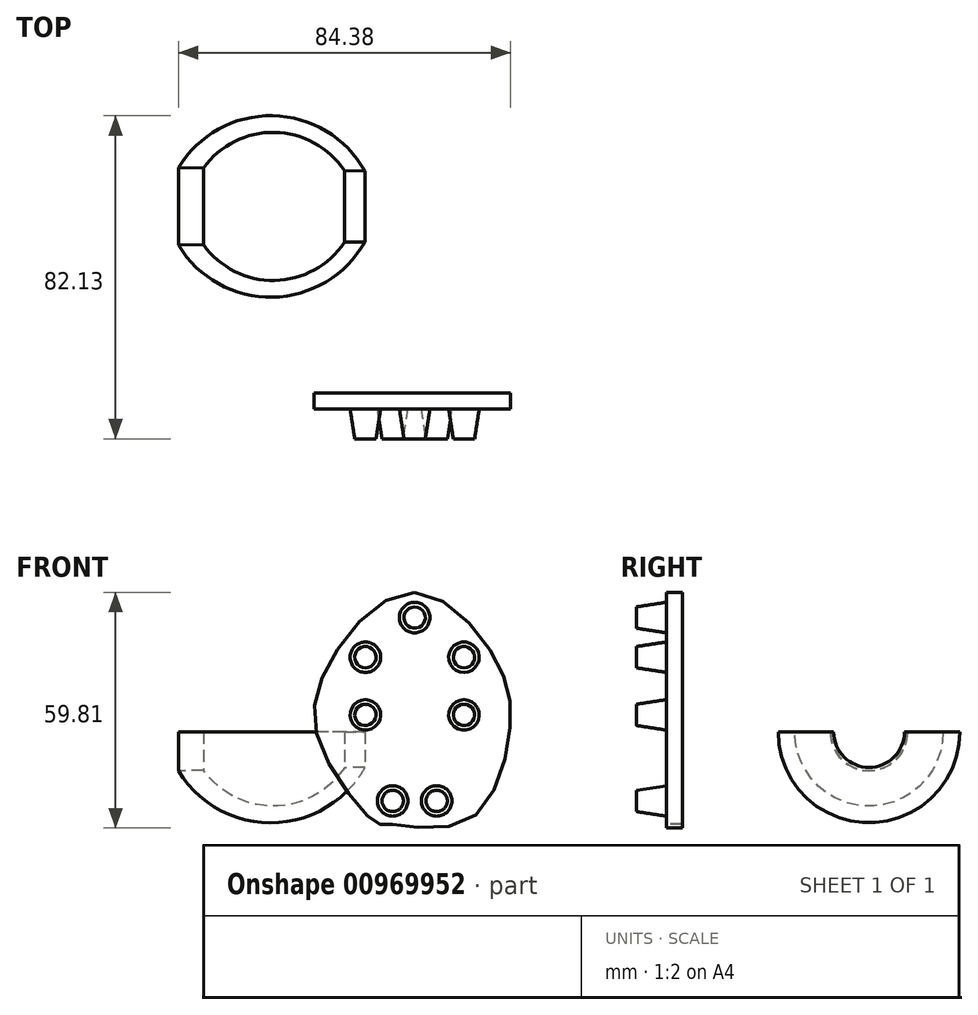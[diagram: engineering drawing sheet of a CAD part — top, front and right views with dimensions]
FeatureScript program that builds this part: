
annotation { "Feature Type Name" : "Feature", "Feature Type Description" : "" }
export const myFeature = defineFeature(function(context is Context, id is Id, definition is map)
    precondition{}
    {
        {
            var Q0;
            Q0=qCreatedBy(makeId("Front.planeOp"),FACE);
            var sketch = newSketch(context, id + "F0", { "sketchPlane" : qUnion([Q0])});
            skCircle(sketch, "E0", {"center": v(0, 29.08) * mm, "radius": 3.88 * mm});
            skSolve(sketch);
        }
        {
            var Q0;
            Q0=qCreatedBy(makeId("Front.planeOp"),FACE);
            cPlane(context, id + "F1", {"entities" : qUnion([Q0]), "cplaneType" : CPlaneType.OFFSET, "offset" : 25.4 * mm, "width" : 152.4 * mm, "height" : 152.4 * mm});
        }
        {
            var Q0;
            Q0=qCreatedBy(id+"F1.planeOp",FACE);
            var sketch = newSketch(context, id + "F2", { "sketchPlane" : qUnion([Q0])});
            skCircle(sketch, "E1", {"center": v(0, 29.1) * mm, "radius": 1.18 * mm});
            skSolve(sketch);
        }
        {
            var Q0;
            Q0=makeQuery(id+"F0.imprint","IMPRINT",FACE,{"disambiguationData":[TD([[makeQuery(id+"F0.imprint","IMPRINT",EDGE,{"derivedFrom":sQuery(id+"F0.wireOp",EDGE,"E0")}),1.0]])]});
            var Q1;
            Q1=sQuery(id+"F2.wireOp",VERTEX,"E1.center");
            loft(context, id + "F3", {"sheetProfilesArray" : [{ "sheetProfileEntities" : qUnion([Q0]) }, { "sheetProfileEntities" : qUnion([Q1]) }]});
        }
        {
            var Q0;
            Q0=qCreatedBy(id+"F1.planeOp",FACE);
            cPlane(context, id + "F4", {"entities" : qUnion([Q0]), "cplaneType" : CPlaneType.OFFSET, "offset" : 17.78 * mm, "oppositeDirection" : true, "width" : 152.4 * mm, "height" : 152.4 * mm});
        }
        {
            var Q0;
            Q0=qCreatedBy(id+"F4.planeOp",FACE);
            var sketch = newSketch(context, id + "F5", { "sketchPlane" : qUnion([Q0])});
            skCircle(sketch, "E2", {"center": v(0, 28.47) * mm, "radius": 5.7 * mm});
            skSolve(sketch);
        }
        {
            var Q0;
            Q0=qCreatedBy(id+"F1.planeOp",FACE);
            var sketch = newSketch(context, id + "F6", { "sketchPlane" : qUnion([Q0])});
            skCircle(sketch, "E3", {"center": v(0, 29.1) * mm, "radius": 3.66 * mm});
            skSolve(sketch);
        }
        {
            var Q1;
            Q1=makeQuery(id+"F5.imprint","IMPRINT",FACE,{"disambiguationData":[TD([[makeQuery(id+"F5.imprint","IMPRINT",EDGE,{"derivedFrom":sQuery(id+"F5.wireOp",EDGE,"E2")}),1.0]])]});
            var Q2;
            Q2=makeQuery(id+"F6.imprint","IMPRINT",FACE,{"disambiguationData":[TD([[makeQuery(id+"F6.imprint","IMPRINT",EDGE,{"derivedFrom":sQuery(id+"F6.wireOp",EDGE,"E3")}),1.0]])]});
            loft(context, id + "F7", {"operationType" : NewBodyOperationType.REMOVE, "sheetProfilesArray" : [{ "sheetProfileEntities" : qUnion([Q1]) }, { "sheetProfileEntities" : qUnion([Q2]) }]});
        }
        {
            var Q0;
            Q0=qCreatedBy(makeId("Front.planeOp"),FACE);
            var sketch = newSketch(context, id + "F8", { "sketchPlane" : qUnion([Q0])});
            skCircle(sketch, "E4", {"center": v(-12.51, 19) * mm, "radius": 3.87 * mm});
            skSolve(sketch);
        }
        {
            var Q0;
            Q0=qCreatedBy(id+"F1.planeOp",FACE);
            var sketch = newSketch(context, id + "F9", { "sketchPlane" : qUnion([Q0])});
            skCircle(sketch, "E5", {"center": v(-12.52, 19.02) * mm, "radius": 3.65 * mm});
            skSolve(sketch);
        }
        {
            var Q0;
            Q0=makeQuery(id+"F8.imprint","IMPRINT",FACE,{"disambiguationData":[TD([[makeQuery(id+"F8.imprint","IMPRINT",EDGE,{"derivedFrom":sQuery(id+"F8.wireOp",EDGE,"E4")}),1.0]])]});
            var Q1;
            Q1=sQuery(id+"F9.wireOp",VERTEX,"E5.center");
            loft(context, id + "F10", {"sheetProfilesArray" : [{ "sheetProfileEntities" : qUnion([Q0]) }, { "sheetProfileEntities" : qUnion([Q1]) }]});
        }
        {
            var Q0;
            Q0=qCreatedBy(id+"F4.planeOp",FACE);
            var sketch = newSketch(context, id + "F11", { "sketchPlane" : qUnion([Q0])});
            skCircle(sketch, "E6", {"center": v(-9.74, 19) * mm, "radius": 7.2 * mm});
            skSolve(sketch);
        }
        {
            var Q0;
            Q0=qCreatedBy(id+"F1.planeOp",FACE);
            var sketch = newSketch(context, id + "F12", { "sketchPlane" : qUnion([Q0])});
            skCircle(sketch, "E7", {"center": v(-23.69, 25.05) * mm, "radius": 56.82 * mm});
            skSolve(sketch);
        }
        {
            var Q1;
            Q1=makeQuery(id+"F11.imprint","IMPRINT",FACE,{"disambiguationData":[TD([[makeQuery(id+"F11.imprint","IMPRINT",EDGE,{"derivedFrom":sQuery(id+"F11.wireOp",EDGE,"E6")}),1.0]])]});
            var Q2;
            Q2=makeQuery(id+"F12.imprint","IMPRINT",FACE,{"disambiguationData":[TD([[makeQuery(id+"F12.imprint","IMPRINT",EDGE,{"derivedFrom":sQuery(id+"F12.wireOp",EDGE,"E7")}),1.0]])]});
            loft(context, id + "F13", {"operationType" : NewBodyOperationType.REMOVE, "sheetProfilesArray" : [{ "sheetProfileEntities" : qUnion([Q1]) }, { "sheetProfileEntities" : qUnion([Q2]) }]});
        }
        {
            var Q0;
            Q0=makeQuery(id+"F10.opLoft","SWEPT_BODY",BODY,{"disambiguationData":[OSD([makeQuery(id+"F8.imprint","IMPRINT",FACE,{"disambiguationData":[TD([[makeQuery(id+"F8.imprint","IMPRINT",EDGE,{"derivedFrom":sQuery(id+"F8.wireOp",EDGE,"E4")}),1.0]])]}),sQuery(id+"F9.wireOp",VERTEX,"E5.center")])]});
            var Q1;
            Q1=qCreatedBy(makeId("Right.planeOp"),FACE);
            mirror(context, id + "F14", {"entities" : qUnion([Q0]), "mirrorPlane" : qUnion([Q1])});
        }
        {
            var Q0;
            Q0=qCreatedBy(makeId("Top.planeOp"),FACE);
            cPlane(context, id + "F15", {"entities" : qUnion([Q0]), "cplaneType" : CPlaneType.OFFSET, "offset" : 11.68 * mm, "width" : 152.4 * mm, "height" : 152.4 * mm});
        }
        {
            var Q0;
            Q0=makeQuery(id+"F10.opLoft","SWEPT_BODY",BODY,{"disambiguationData":[OSD([makeQuery(id+"F8.imprint","IMPRINT",FACE,{"disambiguationData":[TD([[makeQuery(id+"F8.imprint","IMPRINT",EDGE,{"derivedFrom":sQuery(id+"F8.wireOp",EDGE,"E4")}),1.0]])]}),sQuery(id+"F9.wireOp",VERTEX,"E5.center")])]});
            var Q1;
            Q1=makeQuery(id+"F14.opPattern","COPY",BODY,{"derivedFrom":makeQuery(id+"F10.opLoft","SWEPT_BODY",BODY,{"disambiguationData":[OSD([makeQuery(id+"F8.imprint","IMPRINT",FACE,{"disambiguationData":[TD([[makeQuery(id+"F8.imprint","IMPRINT",EDGE,{"derivedFrom":sQuery(id+"F8.wireOp",EDGE,"E4")}),1.0]])]}),sQuery(id+"F9.wireOp",VERTEX,"E5.center")])]}),"instanceName":"1"});
            var Q2;
            Q2=qCreatedBy(id+"F15.planeOp",FACE);
            mirror(context, id + "F16", {"entities" : qUnion([Q0, Q1]), "mirrorPlane" : qUnion([Q2])});
        }
        {
            var Q0;
            Q0=qCreatedBy(makeId("Front.planeOp"),FACE);
            var sketch = newSketch(context, id + "F17", { "sketchPlane" : qUnion([Q0])});
            skCircle(sketch, "E8", {"center": v(-5.59, -17.5) * mm, "radius": 3.88 * mm});
            skSolve(sketch);
        }
        {
            var Q0;
            Q0=qCreatedBy(id+"F1.planeOp",FACE);
            var sketch = newSketch(context, id + "F18", { "sketchPlane" : qUnion([Q0])});
            skCircle(sketch, "E9", {"center": v(-5.59, -17.5) * mm, "radius": 82.5 * mm});
            skSolve(sketch);
        }
        {
            var Q0;
            Q0=makeQuery(id+"F17.imprint","IMPRINT",FACE,{"disambiguationData":[TD([[makeQuery(id+"F17.imprint","IMPRINT",EDGE,{"derivedFrom":sQuery(id+"F17.wireOp",EDGE,"E8")}),1.0]])]});
            var Q1;
            Q1=sQuery(id+"F18.wireOp",VERTEX,"E9.center");
            loft(context, id + "F19", {"sheetProfilesArray" : [{ "sheetProfileEntities" : qUnion([Q0]) }, { "sheetProfileEntities" : qUnion([Q1]) }]});
        }
        {
            var Q0;
            Q0=qCreatedBy(id+"F4.planeOp",FACE);
            var sketch = newSketch(context, id + "F20", { "sketchPlane" : qUnion([Q0])});
            skCircle(sketch, "E10", {"center": v(-10.3, -11.35) * mm, "radius": 53.08 * mm});
            skSolve(sketch);
        }
        {
            var Q0;
            Q0=qCreatedBy(id+"F1.planeOp",FACE);
            var sketch = newSketch(context, id + "F21", { "sketchPlane" : qUnion([Q0])});
            skCircle(sketch, "E11", {"center": v(-5.57, -17.5) * mm, "radius": 4.54 * mm});
            skSolve(sketch);
        }
        {
            var Q0;
            Q0=makeQuery(id+"F20.imprint","IMPRINT",FACE,{"disambiguationData":[TD([[makeQuery(id+"F20.imprint","IMPRINT",EDGE,{"derivedFrom":sQuery(id+"F20.wireOp",EDGE,"E10")}),1.0]])]});
            var Q1;
            Q1=makeQuery(id+"F21.imprint","IMPRINT",FACE,{"disambiguationData":[TD([[makeQuery(id+"F21.imprint","IMPRINT",EDGE,{"derivedFrom":sQuery(id+"F21.wireOp",EDGE,"E11")}),1.0]])]});
            loft(context, id + "F22", {"operationType" : NewBodyOperationType.REMOVE, "sheetProfilesArray" : [{ "sheetProfileEntities" : qUnion([Q0]) }, { "sheetProfileEntities" : qUnion([Q1]) }]});
        }
        {
            var Q0;
            Q0=makeQuery(id+"F19.opLoft","SWEPT_BODY",BODY,{"disambiguationData":[OSD([makeQuery(id+"F17.imprint","IMPRINT",FACE,{"disambiguationData":[TD([[makeQuery(id+"F17.imprint","IMPRINT",EDGE,{"derivedFrom":sQuery(id+"F17.wireOp",EDGE,"E8")}),1.0]])]}),sQuery(id+"F18.wireOp",VERTEX,"E9.center")])]});
            var Q1;
            Q1=qCreatedBy(makeId("Right.planeOp"),FACE);
            mirror(context, id + "F23", {"entities" : qUnion([Q0]), "mirrorPlane" : qUnion([Q1])});
        }
        {
            var Q0;
            Q0=qCreatedBy(makeId("Front.planeOp"),FACE);
            var sketch = newSketch(context, id + "F24", { "sketchPlane" : qUnion([Q0])});
            skFitSpline(sketch, "E12", {"points": [v(0, 35.47) * mm, v(-21.42, 18.05) * mm, v(-23.91, -3.47) * mm, v(-9.87, -23.03) * mm, v(-6.85, -23.38) * mm, v(13.07, -22.67) * mm, v(24.1, 0) * mm, v(20.54, 18.58) * mm, v(0, 35.47) * mm]});
            skSolve(sketch);
        }
        {
            var Q0;
            Q0 = qSketchRegion(id + "F24", true);
            extrude(context, id + "F25", {"entities" : qUnion([Q0]), "oppositeDirection" : true, "depth" : 4.06 * mm, "offsetDistance" : 25.4 * mm});
        }
        {
            var Q0;
            Q0=qCreatedBy(makeId("Top.planeOp"),FACE);
            var sketch = newSketch(context, id + "F26", { "sketchPlane" : qUnion([Q0])});
            skLineSegment(sketch, "E13", {"start": v(-61.6, 51.47) * mm, "end": v(-14.5, 51.47) * mm});
            skLineSegment(sketch, "E14", {"start": v(-14.5, 51.47) * mm, "end": v(-14.5, 51.45) * mm});
            skLineSegment(sketch, "E15", {"start": v(-14.5, 51.45) * mm, "end": v(-61.6, 51.45) * mm});
            skLineSegment(sketch, "E16", {"start": v(-61.6, 51.47) * mm, "end": v(-61.6, 51.45) * mm});
            skSolve(sketch);
        }
        {
            var Q0;
            Q0=qCreatedBy(makeId("Top.planeOp"),FACE);
            var sketch = newSketch(context, id + "F27", { "sketchPlane" : qUnion([Q0])});
            skLineSegment(sketch, "E17", {"start": v(-60.02, 61.31) * mm, "end": v(-16.6, 60.51) * mm});
            skLineSegment(sketch, "E18", {"start": v(-60.02, 61.31) * mm, "end": v(-12.65, 60.44) * mm});
            skLineSegment(sketch, "E19", {"start": v(-12.65, 60.44) * mm, "end": v(-60.02, 61.31) * mm});
            skArc(sketch, "E20", {"start": v(-12.65, 60.44) * mm, "mid": v(-36.08, 74.5) * mm, "end": v(-60.02, 61.31) * mm});
            skSolve(sketch);
        }
        {
            var Q0;
            {var subQ0=sQuery(id+"F27.wireOp",EDGE,"E20");Q0=makeQuery(id+"F27.imprint","IMPRINT",FACE,{"disambiguationData":[TD([[makeQuery(id+"F27.imprint","IMPRINT",EDGE,{"derivedFrom":subQ0}),1.0]])]});}
            var Q1;
            Q1=sQuery(id+"F26.wireOp",EDGE,"E15");
            revolve(context, id + "F28", {"surfaceOperationType" : NewSurfaceOperationType.NEW, "entities" : qUnion([Q0]), "axis" : qUnion([Q1]), "revolveType" : RevolveType.ONE_DIRECTION, "angle" : 180 * degree});
        }
        {
            var Q0;
            Q0=makeQuery(id+"F28.opRevolve","CAP_FACE",FACE,{"disambiguationData":[OSD([sQuery(id+"F27.wireOp",EDGE,"E19"),sQuery(id+"F27.wireOp",EDGE,"E20")])],"isStart":false});
            var sketch = newSketch(context, id + "F29", { "sketchPlane" : qUnion([Q0])});
            skLineSegment(sketch, "E21", {"start": v(-53.63, 41.7) * mm, "end": v(-17.87, 42.37) * mm});
            skArc(sketch, "E22", {"start": v(-53.63, 41.7) * mm, "mid": v(-35.57, 32.63) * mm, "end": v(-17.87, 42.37) * mm});
            skSolve(sketch);
        }
        {
            var Q0;
            Q0 = qSketchRegion(id + "F29", true);
            var Q1;
            Q1=sQuery(id+"F26.wireOp",EDGE,"E15");
            revolve(context, id + "F30", {"operationType" : NewBodyOperationType.REMOVE, "surfaceOperationType" : NewSurfaceOperationType.NEW, "entities" : qUnion([Q0]), "axis" : qUnion([Q1]), "revolveType" : RevolveType.FULL, "oppositeDirection" : true});
        }
    });
